# Revit family: Acoustic-Treatment_Wenger_Absorber-Wall
name_source: partatom
category: Generic Models
revit_build: Autodesk Revit 2016 (Build: 20161004_0715(x64)
units: mm (PartAtom-declared; Revit-internal decimal feet)

## family parameters
Always vertical = No
Can host rebar = No
Cut with Voids When Loaded = No
Part Type = Normal
Room Calculation Point = No
Round Connector Dimension = Use Diameter
Shared = No
Work Plane-Based = Yes

## types (1)
- Acoustic-Treatment_Wenger_Absorber-Wall
    Assembly Code = E1020300
    Construction Details = http://www.arcat.com
    Default Elevation = 0' - 0"
    Description = Wenger Acoustic Product as Specified
    Expected Lifespan (Years) = 0
    Green Building-LEED = http://www.arcat.com
    Keynote = 11 60 01
    Maintenance Schedule (Months) = 0
    Manufacturer = Wenger Corporation
    Manufacturer Website = https://www.wengercorp.com
    Model = As Specified
    Product Data = http://www.arcat.com
    Revision = R1_2017-12
    Sales Information = https://www.wengercorp.com
    SpecWizard = http://www.arcat.com
    Specification = http://www.arcat.com
    Standards Conformance = as Specified
    URL = https://www.wengercorp.com
    Unit Depth = 0' - 2"
    Unit Length = 2' - 8"
    Unit Weight = 0
    Unit Width = 2' - 8"
    Warranty Duration (Years) = 0

## geometry (parser evidence)
native form markers: Sweep x3
no freeform markers — native parametric forms only
